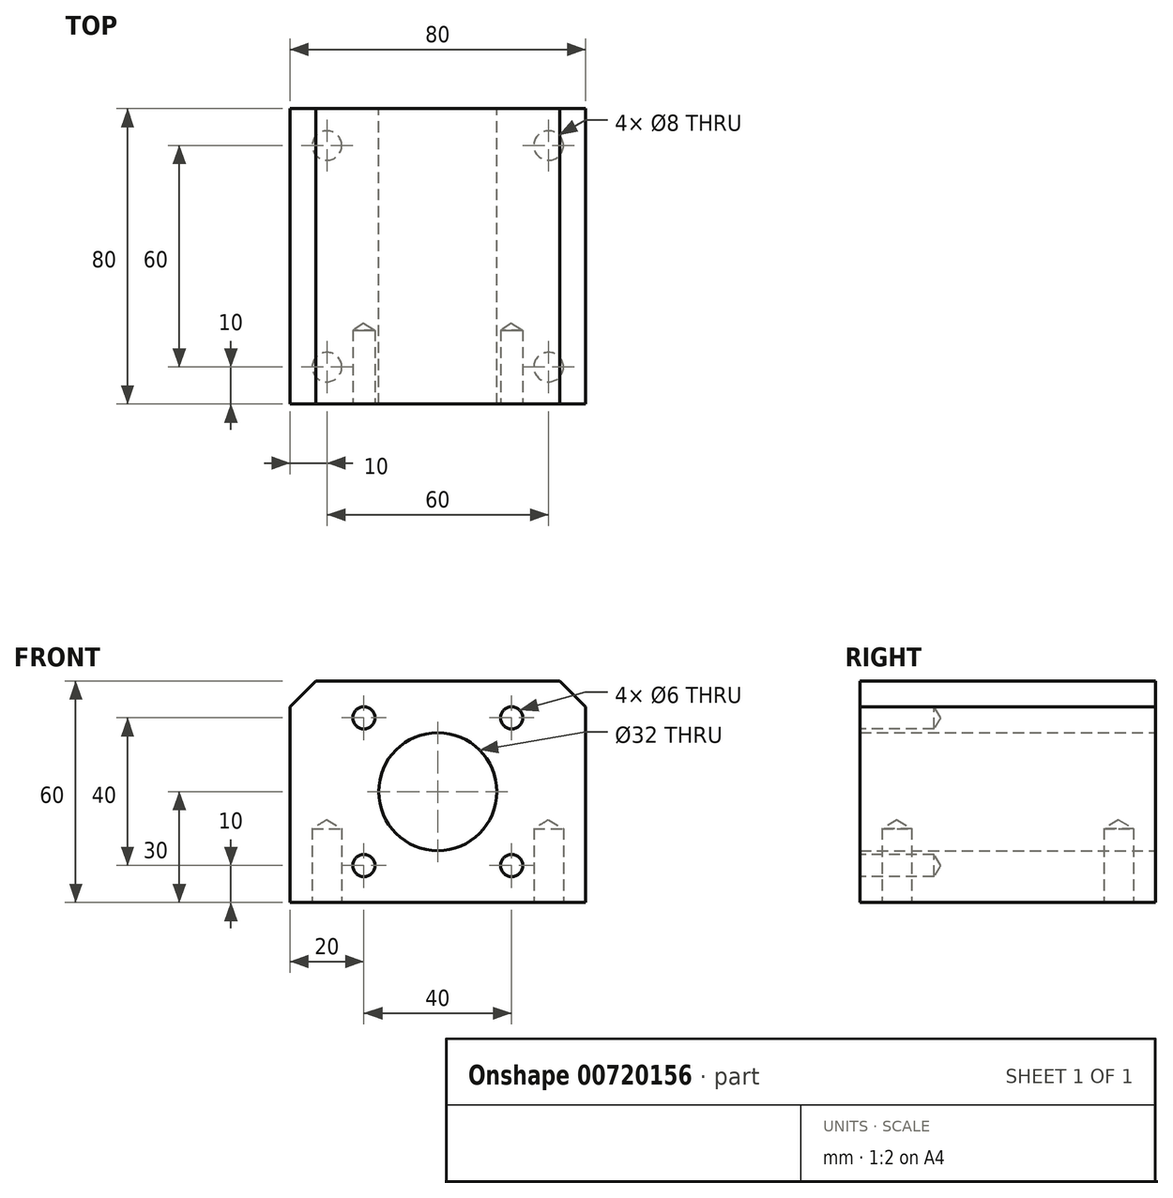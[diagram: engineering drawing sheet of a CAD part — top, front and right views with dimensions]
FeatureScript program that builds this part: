
annotation { "Feature Type Name" : "Feature", "Feature Type Description" : "" }
export const myFeature = defineFeature(function(context is Context, id is Id, definition is map)
    precondition{}
    {
        {
            var Q0;
            Q0=qCreatedBy(makeId("Front.planeOp"),FACE);
            var sketch = newSketch(context, id + "F0", { "sketchPlane" : qUnion([Q0])});
            skLineSegment(sketch, "E0.bottom", {"start": v(0, 0) * mm, "end": v(80, 0) * mm});
            skLineSegment(sketch, "E0.top", {"start": v(0, 60) * mm, "end": v(80, 60) * mm});
            skLineSegment(sketch, "E0.left", {"start": v(0, 0) * mm, "end": v(0, 60) * mm});
            skLineSegment(sketch, "E0.right", {"start": v(80, 0) * mm, "end": v(80, 60) * mm});
            skCircle(sketch, "E1", {"center": v(40, 30) * mm, "radius": 16 * mm});
            skPoint(sketch, "E1.centerSnap0", {"position": v(40, 60) * mm});
            skPoint(sketch, "E1.centerSnap1", {"position": v(0, 30) * mm});
            skSolve(sketch);
        }
        {
            var Q0;
            Q0=makeQuery(id+"F0.imprint","IMPRINT",FACE,{"disambiguationData":[TD([[makeQuery(id+"F0.imprint","IMPRINT",EDGE,{"derivedFrom":sQuery(id+"F0.wireOp",EDGE,"E0.bottom")}),1.0]])]});
            extrude(context, id + "F1", {"entities" : qUnion([Q0]), "depth" : 80 * mm, "offsetDistance" : 25 * mm});
        }
        {
            var Q0;
            Q0=makeQuery(id+"F1.opExtrude","SWEPT_EDGE",EDGE,{"disambiguationData":[OSD([sQuery(id+"F0.wireOp",EDGE,"E0.top"),sQuery(id+"F0.wireOp",EDGE,"E0.left")])]});
            var Q1;
            Q1=makeQuery(id+"F1.opExtrude","SWEPT_EDGE",EDGE,{"disambiguationData":[OSD([sQuery(id+"F0.wireOp",EDGE,"E0.top"),sQuery(id+"F0.wireOp",EDGE,"E0.right")])]});
            chamfer(context, id + "F2", {"entities" : qUnion([Q0, Q1]), "width" : 7 * mm, "tangentPropagation" : true});
        }
        {
            var Q0;
            Q0=makeQuery(id+"F1.opExtrude","CAP_FACE",FACE,{"disambiguationData":[OSD([sQuery(id+"F0.wireOp",EDGE,"E0.bottom"),sQuery(id+"F0.wireOp",EDGE,"E0.top"),sQuery(id+"F0.wireOp",EDGE,"E0.left"),sQuery(id+"F0.wireOp",EDGE,"E0.right"),sQuery(id+"F0.wireOp",EDGE,"E1")])],"isStart":false});
            var sketch = newSketch(context, id + "F3", { "sketchPlane" : qUnion([Q0])});
            skPoint(sketch, "E2", {"position": v(20, 50) * mm});
            skPoint(sketch, "E3", {"position": v(60, 50) * mm});
            skPoint(sketch, "E4", {"position": v(20, 10) * mm});
            skPoint(sketch, "E5", {"position": v(60, 10) * mm});
            skSolve(sketch);
        }
        {
            var Q0;
            Q0=sQuery(id+"F3.wireOp",VERTEX,"E2");
            var Q1;
            Q1=sQuery(id+"F3.wireOp",VERTEX,"E3");
            var Q2;
            Q2=sQuery(id+"F3.wireOp",VERTEX,"E5");
            var Q3;
            Q3=sQuery(id+"F3.wireOp",VERTEX,"E4");
            var Q4;
            Q4=makeQuery(id+"F1.opExtrude","SWEPT_BODY",BODY,{"disambiguationData":[OSD([sQuery(id+"F0.wireOp",EDGE,"E0.bottom"),sQuery(id+"F0.wireOp",EDGE,"E0.top"),sQuery(id+"F0.wireOp",EDGE,"E0.left"),sQuery(id+"F0.wireOp",EDGE,"E0.right"),sQuery(id+"F0.wireOp",EDGE,"E1")])]});
            hole(context, id + "F4", {"style" : HoleStyle.SIMPLE, "endStyle" : HoleEndStyle.BLIND, "holeDiameter" : 6 * mm, "majorDiameter" : 5 * mm, "holeDepth" : 20 * mm, "isTappedThrough" : true, "tappedDepth" : 12 * mm, "tapClearance" : 3, "startFromSketch" : true, "locations" : qUnion([Q0, Q1, Q2, Q3]), "scope" : qUnion([Q4])});
        }
        {
            var Q0;
            Q0=makeQuery(id+"F1.opExtrude","SWEPT_FACE",FACE,{"disambiguationData":[OSD([sQuery(id+"F0.wireOp",EDGE,"E0.bottom")])]});
            var sketch = newSketch(context, id + "F5", { "sketchPlane" : qUnion([Q0])});
            skPoint(sketch, "E6", {"position": v(10, 70) * mm});
            skPoint(sketch, "E7.0.1.0", {"position": v(10, 10) * mm});
            skPoint(sketch, "E7.1.0.0", {"position": v(70, 70) * mm});
            skPoint(sketch, "E7.1.1.0", {"position": v(70, 10) * mm});
            skLineSegment(sketch, "E7.direction2", {"start": v(10, 70) * mm, "end": v(10, 10) * mm, "construction": true});
            skSolve(sketch);
        }
        {
            var Q0;
            Q0=sQuery(id+"F5.wireOp",VERTEX,"E6");
            var Q1;
            Q1=sQuery(id+"F5.wireOp",VERTEX,"E7.1.0.0");
            var Q2;
            Q2=sQuery(id+"F5.wireOp",VERTEX,"E7.1.1.0");
            var Q3;
            Q3=sQuery(id+"F5.wireOp",VERTEX,"E7.0.1.0");
            var Q4;
            Q4=makeQuery(id+"F1.opExtrude","SWEPT_BODY",BODY,{"disambiguationData":[OSD([sQuery(id+"F0.wireOp",EDGE,"E0.bottom"),sQuery(id+"F0.wireOp",EDGE,"E0.top"),sQuery(id+"F0.wireOp",EDGE,"E0.left"),sQuery(id+"F0.wireOp",EDGE,"E0.right"),sQuery(id+"F0.wireOp",EDGE,"E1")])]});
            hole(context, id + "F6", {"style" : HoleStyle.SIMPLE, "endStyle" : HoleEndStyle.BLIND, "holeDiameter" : 8 * mm, "majorDiameter" : 5 * mm, "holeDepth" : 20 * mm, "isTappedThrough" : true, "tappedDepth" : 12 * mm, "tapClearance" : 3, "startFromSketch" : true, "locations" : qUnion([Q0, Q1, Q2, Q3]), "scope" : qUnion([Q4])});
        }
    });
